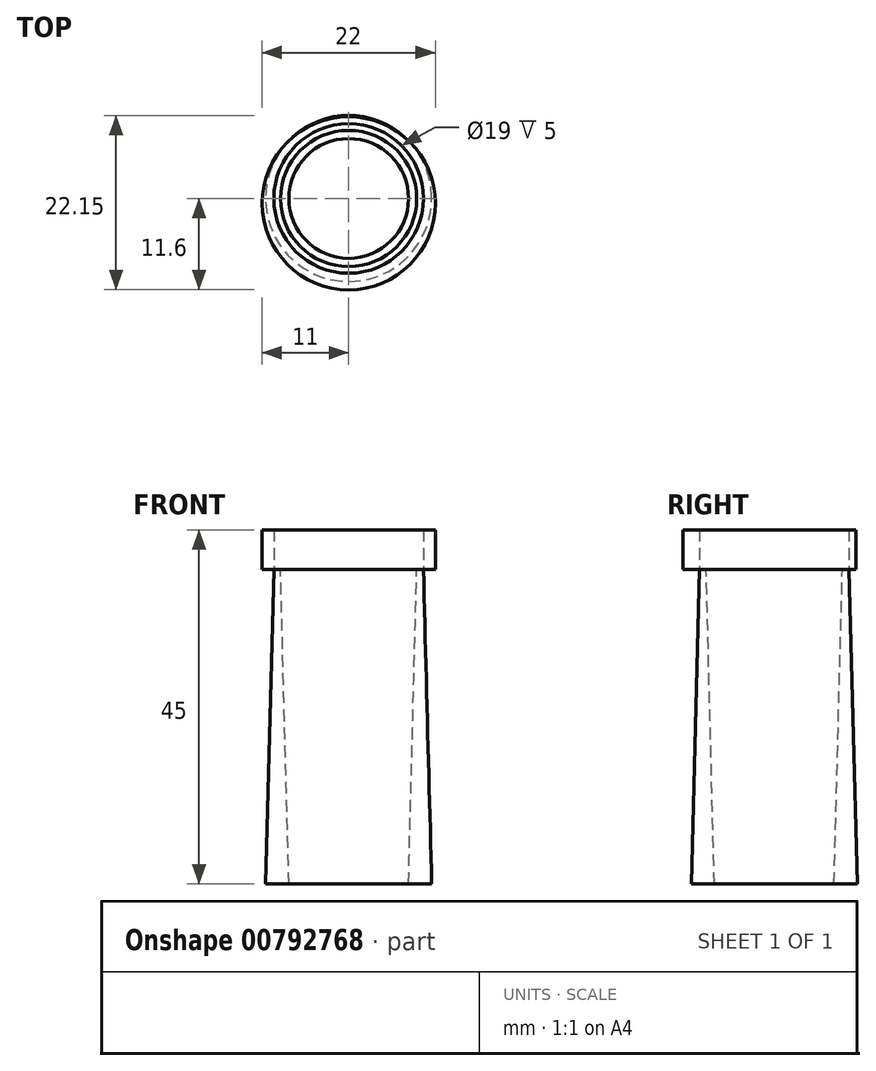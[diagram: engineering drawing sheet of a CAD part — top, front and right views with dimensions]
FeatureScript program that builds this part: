
annotation { "Feature Type Name" : "Feature", "Feature Type Description" : "" }
export const myFeature = defineFeature(function(context is Context, id is Id, definition is map)
    precondition{}
    {
        {
            var Q0;
            Q0=qCreatedBy(makeId("Top.planeOp"),FACE);
            var sketch = newSketch(context, id + "F0", { "sketchPlane" : qUnion([Q0])});
            skCircle(sketch, "E0", {"center": v(0, 0) * mm, "radius": 9.5 * mm});
            skCircle(sketch, "E1", {"center": v(0, 0) * mm, "radius": 8.65 * mm});
            skCircle(sketch, "E2", {"center": v(0, -0.6) * mm, "radius": 11 * mm});
            skSolve(sketch);
        }
        {
            var Q0;
            Q0=makeQuery(id+"F0.imprint","IMPRINT",FACE,{"disambiguationData":[TD([[makeQuery(id+"F0.imprint","IMPRINT",EDGE,{"derivedFrom":sQuery(id+"F0.wireOp",EDGE,"E0")}),1.0]])]});
            extrude(context, id + "F1", {"entities" : qUnion([Q0]), "oppositeDirection" : true, "depth" : 40 * mm, "offsetDistance" : 25 * mm, "hasDraft" : true, "draftAngle" : 1.5 * degree});
        }
        {
            var Q0;
            Q0 = qSketchRegion(id + "F0", true);
            extrude(context, id + "F2", {"entities" : qUnion([Q0]), "operationType" : NewBodyOperationType.ADD, "depth" : 5 * mm, "offsetDistance" : 25 * mm});
        }
    });
